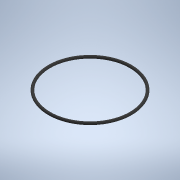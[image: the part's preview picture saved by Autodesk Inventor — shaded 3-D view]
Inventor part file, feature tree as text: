
AUTODESK INVENTOR PART (.ipt)
format: ipt  version: 2020.3 (Build 243373000, 373)  size: 115,200 bytes
history: native  units: mm
features: revolve x1, sketch x1
ambient origin geometry x8: Origin, YZ Plane, XZ Plane, XY Plane, X Axis, Y Axis, Z Axis, Center Point
bodies: Solid1 (feature_tree)
feature tree (2):
  revolve  "Revolution1"  [1 undecoded]
  sketch  "Sketch1"  dims[d0=2.62mm d1=40.81mm d2=90.0deg]
note: 1 required parameter value undecoded (feature->parameter linkage not recoverable at this tier; creation-order binding heuristic only, values carry confidence <= 0.55)
